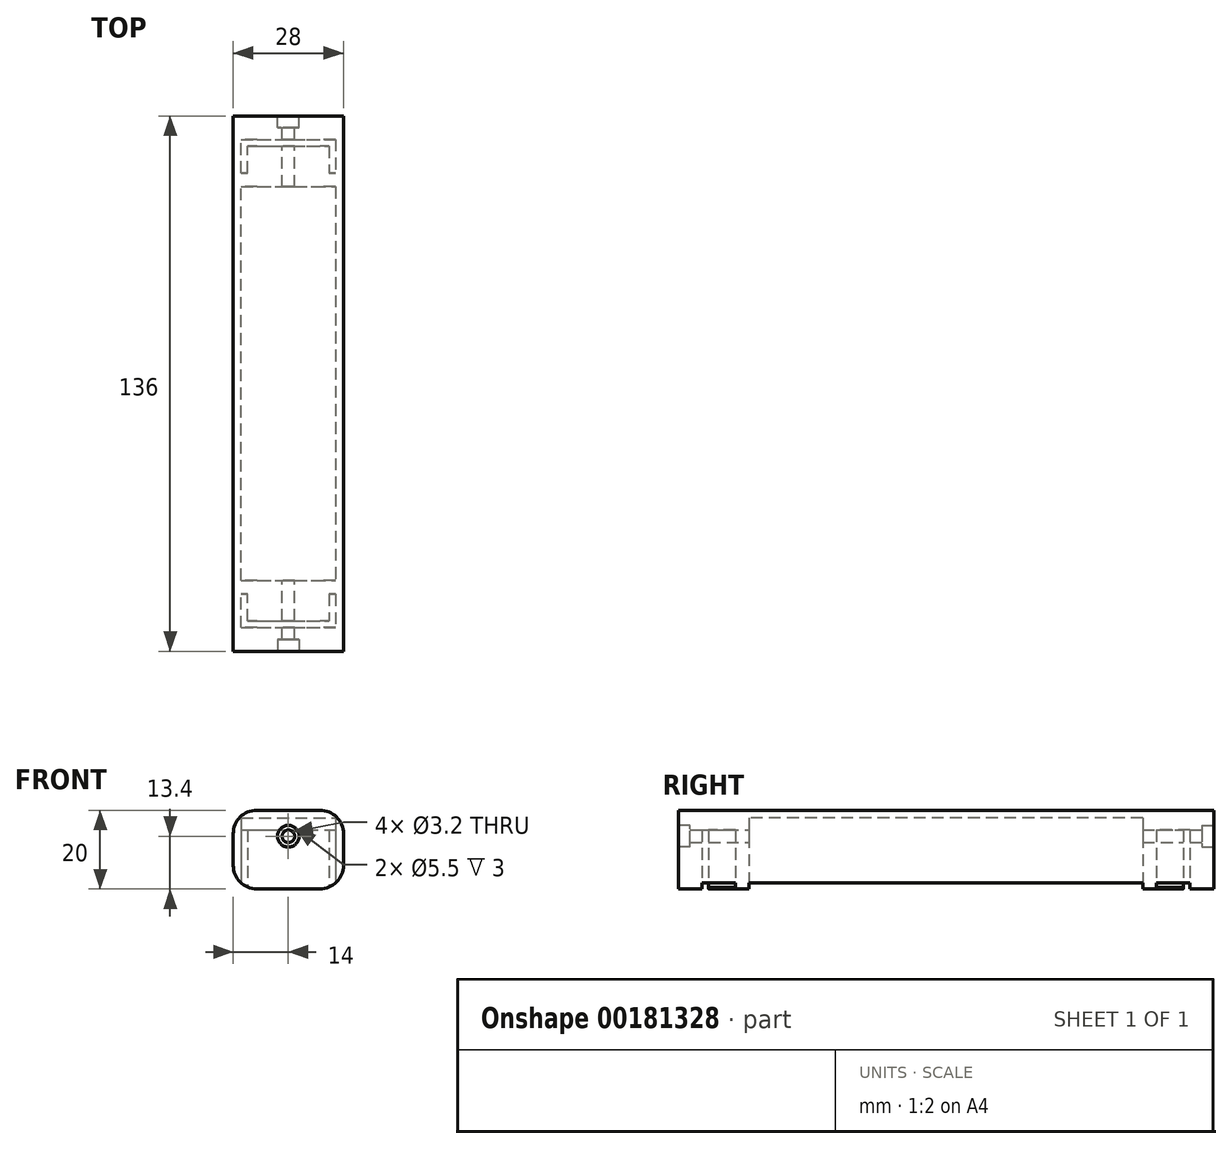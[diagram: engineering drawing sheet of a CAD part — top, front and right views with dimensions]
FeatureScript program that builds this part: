
annotation { "Feature Type Name" : "Feature", "Feature Type Description" : "" }
export const myFeature = defineFeature(function(context is Context, id is Id, definition is map)
    precondition{}
    {
        {
            var Q0;
            Q0=qCreatedBy(makeId("Front.planeOp"),FACE);
            var sketch = newSketch(context, id + "F0", { "sketchPlane" : qUnion([Q0])});
            skLineSegment(sketch, "E0.bottom", {"start": v(-14, 10) * mm, "end": v(14, 10) * mm});
            skLineSegment(sketch, "E0.top", {"start": v(-14, -10) * mm, "end": v(14, -10) * mm});
            skLineSegment(sketch, "E0.left", {"start": v(-14, 10) * mm, "end": v(-14, -10) * mm});
            skLineSegment(sketch, "E0.right", {"start": v(14, 10) * mm, "end": v(14, -10) * mm});
            skSolve(sketch);
        }
        {
            var Q0;
            Q0=makeQuery(id+"F0.imprint","IMPRINT",FACE,{"disambiguationData":[TD([[makeQuery(id+"F0.imprint","IMPRINT",EDGE,{"derivedFrom":sQuery(id+"F0.wireOp",EDGE,"E0.bottom")}),-1.0]])]});
            extrude(context, id + "F1", {"entities" : qUnion([Q0]), "endBound" : BoundingType.SYMMETRIC, "depth" : 136 * mm});
        }
        {
            var Q0;
            Q0=makeQuery(id+"F1.opExtrude","SWEPT_FACE",FACE,{"disambiguationData":[OSD([sQuery(id+"F0.wireOp",EDGE,"E0.top")])]});
            var sketch = newSketch(context, id + "F2", { "sketchPlane" : qUnion([Q0])});
            skLineSegment(sketch, "E1.bottom", {"start": v(-12, 62) * mm, "end": v(12, 62) * mm});
            skLineSegment(sketch, "E1.top", {"start": v(-12, 53.5) * mm, "end": v(-10.3, 53.5) * mm});
            skLineSegment(sketch, "E1.left", {"start": v(-12, 62) * mm, "end": v(-12, 53.5) * mm});
            skLineSegment(sketch, "E1.right", {"start": v(12, 62) * mm, "end": v(12, 53.5) * mm});
            skLineSegment(sketch, "E2.top", {"start": v(-10.3, 60.3) * mm, "end": v(10.3, 60.3) * mm});
            skLineSegment(sketch, "E2.left", {"start": v(-10.3, 53.5) * mm, "end": v(-10.3, 60.3) * mm});
            skLineSegment(sketch, "E2.right", {"start": v(10.3, 53.5) * mm, "end": v(10.3, 60.3) * mm});
            skLineSegment(sketch, "E3.trimOffspring", {"start": v(10.3, 53.5) * mm, "end": v(12, 53.5) * mm});
            skLineSegment(sketch, "E4.MirrorCS", {"start": v(-12, -62) * mm, "end": v(-12, -53.5) * mm});
            skLineSegment(sketch, "E5.MirrorCS", {"start": v(-12, -62) * mm, "end": v(12, -62) * mm});
            skLineSegment(sketch, "E6.MirrorCS", {"start": v(12, -62) * mm, "end": v(12, -53.5) * mm});
            skLineSegment(sketch, "E7.MirrorCS", {"start": v(10.3, -53.5) * mm, "end": v(10.3, -60.3) * mm});
            skLineSegment(sketch, "E8.MirrorCS", {"start": v(10.3, -53.5) * mm, "end": v(12, -53.5) * mm});
            skLineSegment(sketch, "E9.MirrorCS", {"start": v(-10.3, -60.3) * mm, "end": v(10.3, -60.3) * mm});
            skLineSegment(sketch, "E10.MirrorCS", {"start": v(-10.3, -53.5) * mm, "end": v(-10.3, -60.3) * mm});
            skLineSegment(sketch, "E11.MirrorCS", {"start": v(-12, -53.5) * mm, "end": v(-10.3, -53.5) * mm});
            skLineSegment(sketch, "E12.bottom", {"start": v(-12, -50) * mm, "end": v(12, -50) * mm});
            skLineSegment(sketch, "E12.top", {"start": v(-12, 50) * mm, "end": v(12, 50) * mm});
            skLineSegment(sketch, "E12.left", {"start": v(-12, -50) * mm, "end": v(-12, 50) * mm});
            skLineSegment(sketch, "E12.right", {"start": v(12, -50) * mm, "end": v(12, 50) * mm});
            skSolve(sketch);
        }
        {
            var Q0;
            Q0=makeQuery(id+"F2.imprint","IMPRINT",FACE,{"disambiguationData":[TD([[makeQuery(id+"F2.imprint","IMPRINT",EDGE,{"derivedFrom":sQuery(id+"F2.wireOp",EDGE,"E1.bottom")}),-1.0]])]});
            var Q1;
            Q1=makeQuery(id+"F2.imprint","IMPRINT",FACE,{"disambiguationData":[TD([[makeQuery(id+"F2.imprint","IMPRINT",EDGE,{"derivedFrom":sQuery(id+"F2.wireOp",EDGE,"E4.MirrorCS")}),-1.0]])]});
            extrude(context, id + "F3", {"entities" : qUnion([Q0, Q1]), "operationType" : NewBodyOperationType.REMOVE, "oppositeDirection" : true, "depth" : 15 * mm});
        }
        {
            var Q0;
            Q0=makeQuery(id+"F2.imprint","IMPRINT",FACE,{"disambiguationData":[TD([[makeQuery(id+"F2.imprint","IMPRINT",EDGE,{"derivedFrom":sQuery(id+"F2.wireOp",EDGE,"E12.bottom")}),1.0]])]});
            extrude(context, id + "F4", {"entities" : qUnion([Q0]), "operationType" : NewBodyOperationType.REMOVE, "oppositeDirection" : true, "depth" : 18 * mm});
        }
        {
            var Q0;
            Q0=makeQuery(id+"F1.opExtrude","SWEPT_EDGE",EDGE,{"disambiguationData":[OSD([sQuery(id+"F0.wireOp",EDGE,"E0.bottom"),sQuery(id+"F0.wireOp",EDGE,"E0.left")])]});
            var Q1;
            Q1=makeQuery(id+"F1.opExtrude","SWEPT_EDGE",EDGE,{"disambiguationData":[OSD([sQuery(id+"F0.wireOp",EDGE,"E0.bottom"),sQuery(id+"F0.wireOp",EDGE,"E0.right")])]});
            var Q2;
            Q2=makeQuery(id+"F1.opExtrude","SWEPT_EDGE",EDGE,{"disambiguationData":[OSD([sQuery(id+"F0.wireOp",EDGE,"E0.top"),sQuery(id+"F0.wireOp",EDGE,"E0.right")])]});
            var Q3;
            Q3=makeQuery(id+"F1.opExtrude","SWEPT_EDGE",EDGE,{"disambiguationData":[OSD([sQuery(id+"F0.wireOp",EDGE,"E0.top"),sQuery(id+"F0.wireOp",EDGE,"E0.left")])]});
            fillet(context, id + "F5", {"entities" : qUnion([Q0, Q1, Q2, Q3]), "radius" : 6 * mm, "tangentPropagation" : true, "allowEdgeOverflow" : false});
        }
        {
            var Q0;
            Q0=makeQuery(id+"F1.opExtrude","CAP_FACE",FACE,{"disambiguationData":[OSD([sQuery(id+"F0.wireOp",EDGE,"E0.bottom"),sQuery(id+"F0.wireOp",EDGE,"E0.top"),sQuery(id+"F0.wireOp",EDGE,"E0.left"),sQuery(id+"F0.wireOp",EDGE,"E0.right")])],"isStart":true});
            var sketch = newSketch(context, id + "F6", { "sketchPlane" : qUnion([Q0])});
            skCircle(sketch, "E13", {"center": v(0, 3.4) * mm, "radius": 1.6 * mm});
            skCircle(sketch, "E14", {"center": v(0, 3.4) * mm, "radius": 2.75 * mm});
            skSolve(sketch);
        }
        {
            var Q0;
            Q0=makeQuery(id+"F6.imprint","IMPRINT",FACE,{"disambiguationData":[TD([[makeQuery(id+"F6.imprint","IMPRINT",EDGE,{"derivedFrom":sQuery(id+"F6.wireOp",EDGE,"E13")}),1.0]])]});
            extrude(context, id + "F7", {"entities" : qUnion([Q0]), "operationType" : NewBodyOperationType.REMOVE, "oppositeDirection" : true, "depth" : 140 * mm});
        }
        {
            var Q0;
            Q0=makeQuery(id+"F6.imprint","IMPRINT",FACE,{"disambiguationData":[TD([[makeQuery(id+"F6.imprint","IMPRINT",EDGE,{"derivedFrom":sQuery(id+"F6.wireOp",EDGE,"E13")}),-1.0]])]});
            extrude(context, id + "F8", {"entities" : qUnion([Q0]), "operationType" : NewBodyOperationType.REMOVE, "oppositeDirection" : true, "depth" : 3 * mm});
        }
        {
            var Q0;
            Q0=makeQuery(id+"F1.opExtrude","CAP_FACE",FACE,{"disambiguationData":[OSD([sQuery(id+"F0.wireOp",EDGE,"E0.bottom"),sQuery(id+"F0.wireOp",EDGE,"E0.top"),sQuery(id+"F0.wireOp",EDGE,"E0.left"),sQuery(id+"F0.wireOp",EDGE,"E0.right")])],"isStart":false});
            var sketch = newSketch(context, id + "F9", { "sketchPlane" : qUnion([Q0])});
            skCircle(sketch, "E15", {"center": v(0, 3.4) * mm, "radius": 2.75 * mm});
            skSolve(sketch);
        }
        {
            var Q0;
            Q0=makeQuery(id+"F9.imprint","IMPRINT",FACE,{"disambiguationData":[TD([[makeQuery(id+"F9.imprint","IMPRINT",EDGE,{"derivedFrom":sQuery(id+"F9.wireOp",EDGE,"E15")}),1.0]])]});
            extrude(context, id + "F10", {"entities" : qUnion([Q0]), "operationType" : NewBodyOperationType.REMOVE, "oppositeDirection" : true, "depth" : 3 * mm});
        }
    });
